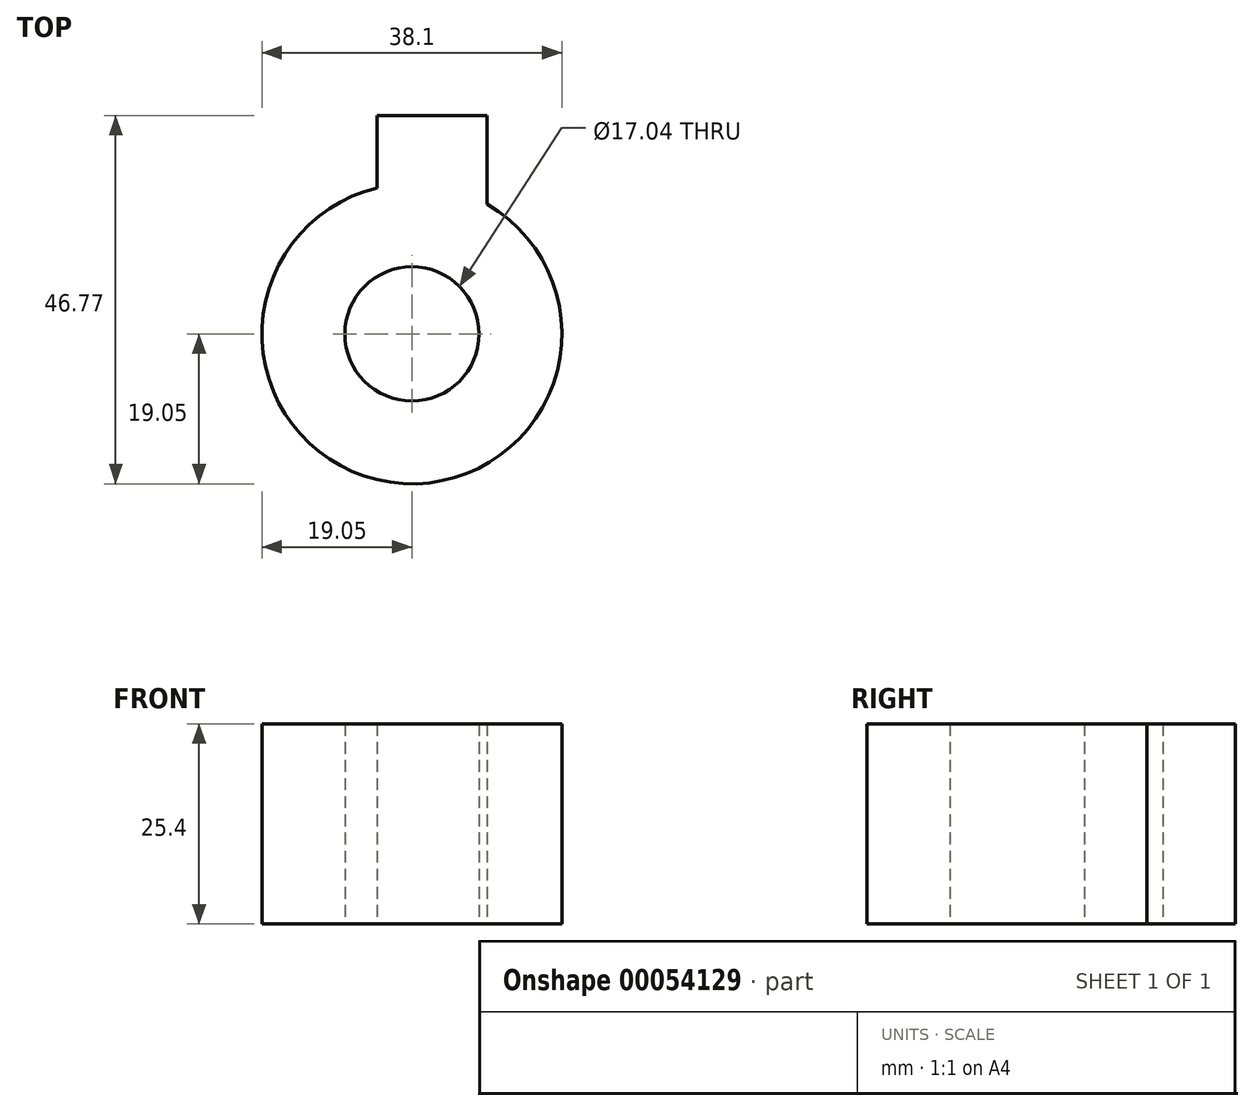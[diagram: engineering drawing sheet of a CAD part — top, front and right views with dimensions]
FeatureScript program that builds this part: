
annotation { "Feature Type Name" : "Feature", "Feature Type Description" : "" }
export const myFeature = defineFeature(function(context is Context, id is Id, definition is map)
    precondition{}
    {
        {
            var Q0;
            Q0=qCreatedBy(makeId("Top.planeOp"),FACE);
            var sketch = newSketch(context, id + "F0", { "sketchPlane" : qUnion([Q0])});
            skCircle(sketch, "E0", {"center": v(0, 0) * mm, "radius": 19.05 * mm});
            skLineSegment(sketch, "E1", {"start": v(-4.4, 18.53) * mm, "end": v(-4.4, 27.72) * mm});
            skLineSegment(sketch, "E2", {"start": v(9.57, 16.47) * mm, "end": v(9.57, 27.72) * mm});
            skLineSegment(sketch, "E3", {"start": v(-4.4, 27.72) * mm, "end": v(9.57, 27.72) * mm});
            skCircle(sketch, "E4", {"center": v(0, 0) * mm, "radius": 8.52 * mm});
            skSolve(sketch);
        }
        {
            var Q0;
            Q0 = qSketchRegion(id + "F0", true);
            extrude(context, id + "F1", {"entities" : qUnion([Q0]), "depth" : 25.4 * mm});
        }
    });
